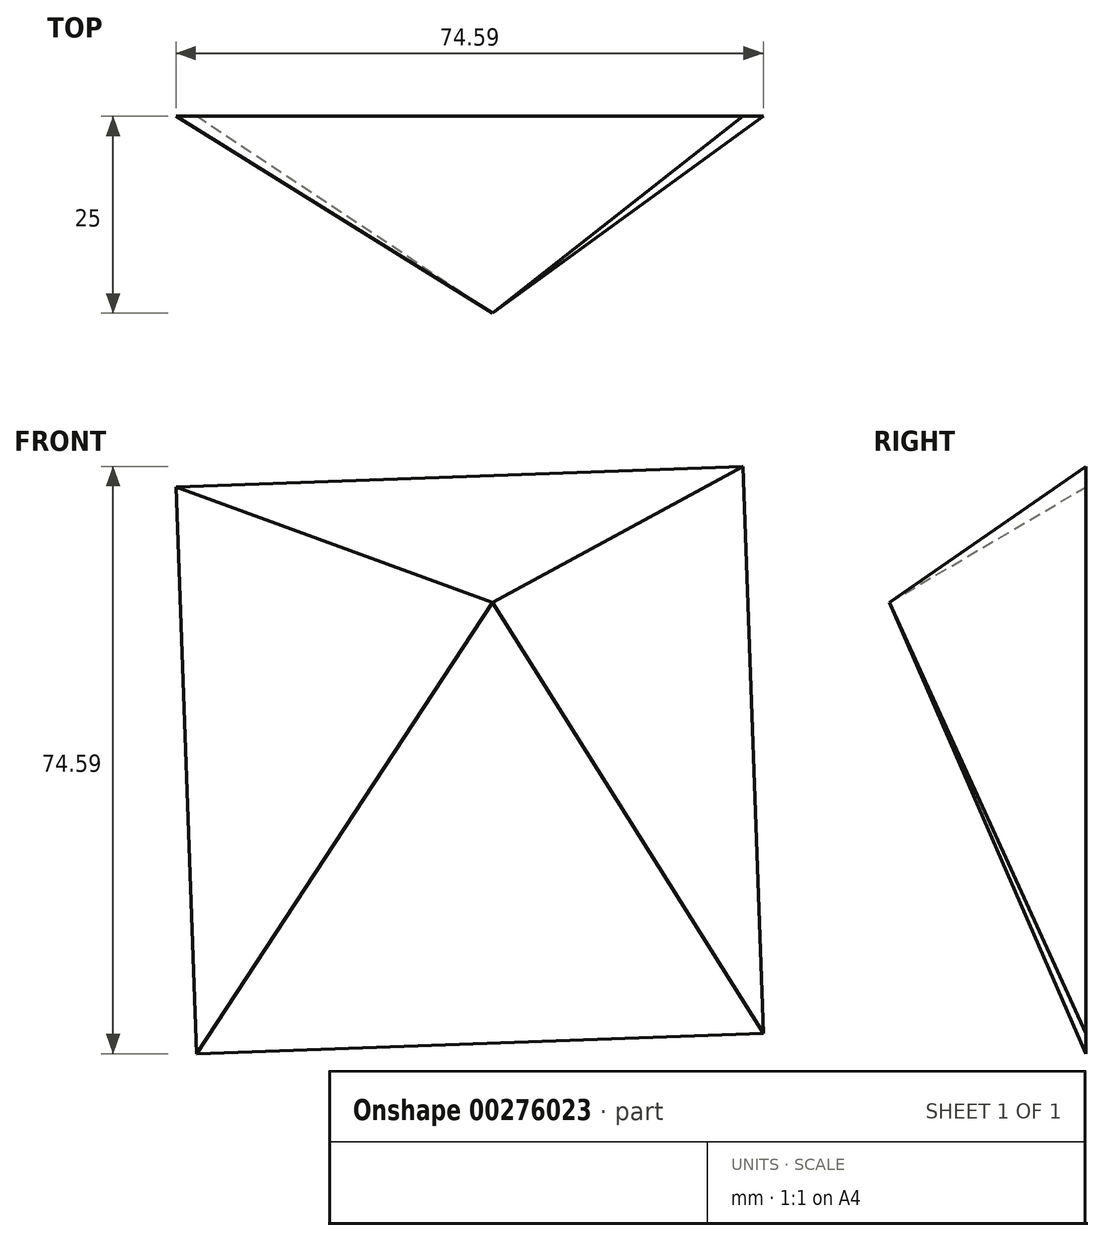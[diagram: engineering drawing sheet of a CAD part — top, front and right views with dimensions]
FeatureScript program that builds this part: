
annotation { "Feature Type Name" : "Feature", "Feature Type Description" : "" }
export const myFeature = defineFeature(function(context is Context, id is Id, definition is map)
    precondition{}
    {
        {
            var Q0;
            Q0=qCreatedBy(makeId("Front.planeOp"),FACE);
            var sketch = newSketch(context, id + "F0", { "sketchPlane" : qUnion([Q0])});
            skCircle(sketch, "E0.cCircle", {"center": v(-16.35, 20.51) * mm, "radius": 50.95 * mm, "construction": true});
            skLineSegment(sketch, "E0.0", {"start": v(20.94, -14.2) * mm, "end": v(-51.07, -16.78) * mm});
            skLineSegment(sketch, "E0.1", {"start": v(-51.07, -16.78) * mm, "end": v(-53.65, 55.23) * mm});
            skLineSegment(sketch, "E0.2", {"start": v(-53.65, 55.23) * mm, "end": v(18.36, 57.8) * mm});
            skLineSegment(sketch, "E0.3", {"start": v(18.36, 57.8) * mm, "end": v(20.94, -14.2) * mm});
            skSolve(sketch);
        }
        {
            var Q0;
            Q0=qCreatedBy(makeId("Front.planeOp"),FACE);
            cPlane(context, id + "F1", {"entities" : qUnion([Q0]), "cplaneType" : CPlaneType.OFFSET, "offset" : 25 * mm, "width" : 150 * mm, "height" : 150 * mm});
        }
        {
            var Q0;
            Q0=qCreatedBy(id+"F1.planeOp",FACE);
            var sketch = newSketch(context, id + "F2", { "sketchPlane" : qUnion([Q0])});
            skPoint(sketch, "E1", {"position": v(-13.49, 40.54) * mm});
            skSolve(sketch);
        }
        {
            var Q0;
            Q0=sQuery(id+"F2.wireOp",VERTEX,"E1");
            var Q1;
            Q1=makeQuery(id+"F0.imprint","IMPRINT",FACE,{"disambiguationData":[TD([[makeQuery(id+"F0.imprint","IMPRINT",EDGE,{"derivedFrom":sQuery(id+"F0.wireOp",EDGE,"E0.0")}),-1.0]])]});
            loft(context, id + "F3", {"sheetProfilesArray" : [{ "sheetProfileEntities" : qUnion([Q0]) }, { "sheetProfileEntities" : qUnion([Q1]) }]});
        }
    });
